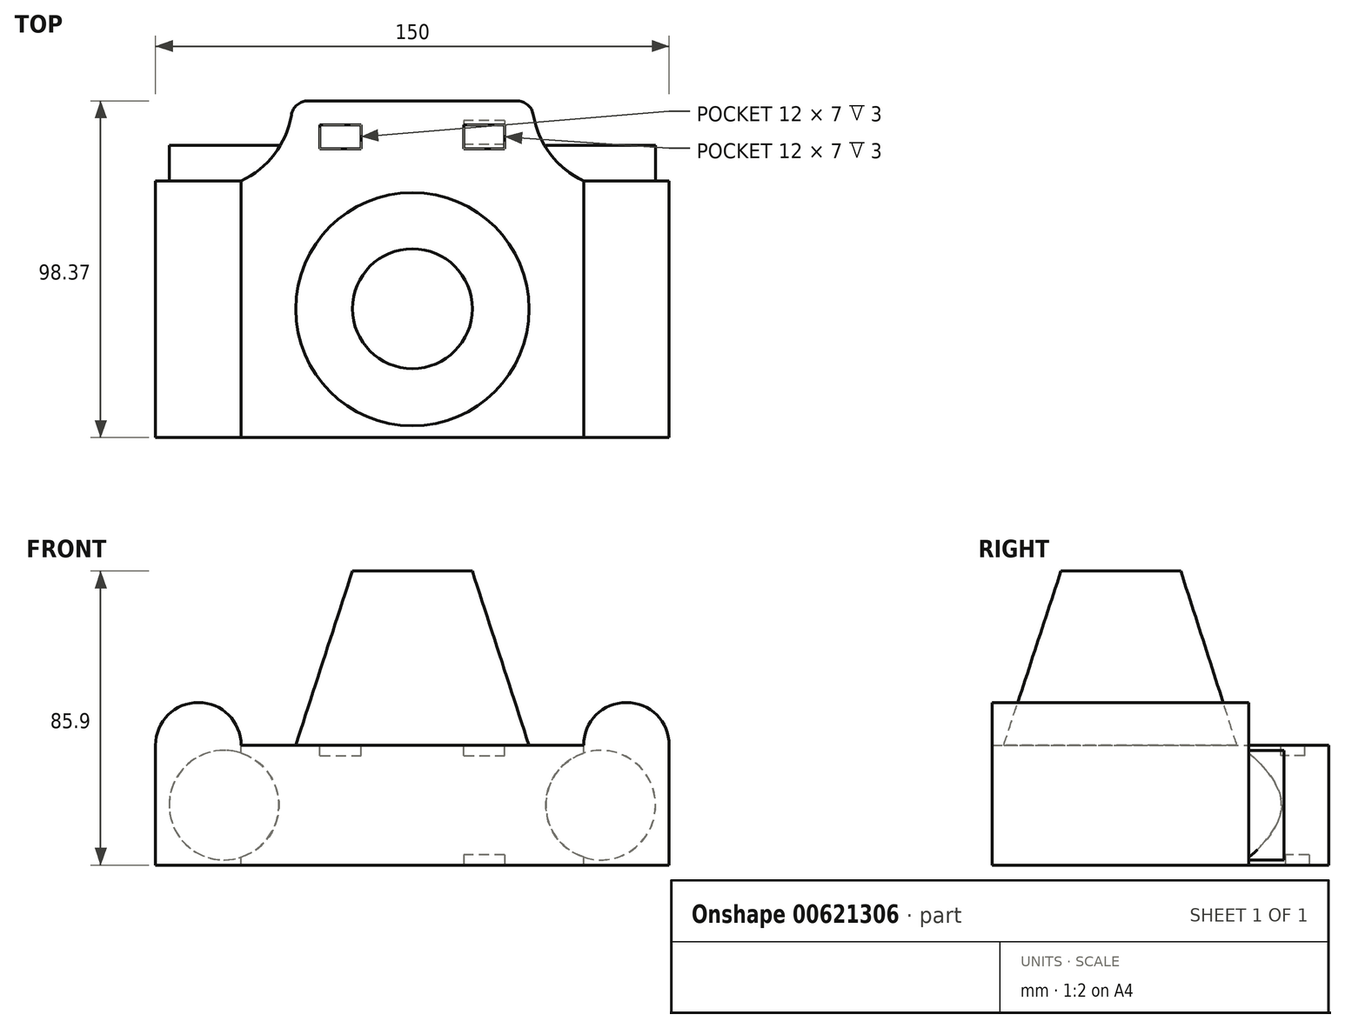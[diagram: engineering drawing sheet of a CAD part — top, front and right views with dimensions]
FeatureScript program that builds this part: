
annotation { "Feature Type Name" : "Feature", "Feature Type Description" : "" }
export const myFeature = defineFeature(function(context is Context, id is Id, definition is map)
    precondition{}
    {
        {
            var Q0;
            Q0=qCreatedBy(makeId("Front.planeOp"),FACE);
            var sketch = newSketch(context, id + "F0", { "sketchPlane" : qUnion([Q0])});
            skLineSegment(sketch, "E0.bottom", {"start": v(75, 17.5) * mm, "end": v(-75, 17.5) * mm});
            skLineSegment(sketch, "E0.top", {"start": v(75, -17.5) * mm, "end": v(-75, -17.5) * mm});
            skLineSegment(sketch, "E0.left", {"start": v(75, 17.5) * mm, "end": v(75, -17.5) * mm});
            skLineSegment(sketch, "E0.right", {"start": v(-75, 17.5) * mm, "end": v(-75, -17.5) * mm});
            skPoint(sketch, "E0.middle", {"position": v(0, 0) * mm});
            skArc(sketch, "E1", {"start": v(-50, 17.5) * mm, "mid": v(-62.5, 30) * mm, "end": v(-75, 17.5) * mm});
            skArc(sketch, "E2", {"start": v(75, 17.5) * mm, "mid": v(62.5, 30) * mm, "end": v(50, 17.5) * mm});
            skSolve(sketch);
        }
        {
            var Q0;
            Q0 = qSketchRegion(id + "F0", true);
            extrude(context, id + "F1", {"entities" : qUnion([Q0]), "depth" : 75 * mm, "offsetDistance" : 25 * mm});
        }
        {
            var Q0;
            Q0=makeQuery(id+"F1.opExtrude","SWEPT_FACE",FACE,{"disambiguationData":[OSD([sQuery(id+"F0.wireOp",EDGE,"E0.bottom")])]});
            var sketch = newSketch(context, id + "F2", { "sketchPlane" : qUnion([Q0])});
            skLineSegment(sketch, "E3", {"start": v(0, 0) * mm, "end": v(0, -75) * mm, "construction": true});
            skCircle(sketch, "E4", {"center": v(0, -37.5) * mm, "radius": 34.05 * mm});
            skSolve(sketch);
        }
        {
            var Q0;
            Q0=makeQuery(id+"F2.imprint","IMPRINT",FACE,{"disambiguationData":[TD([[makeQuery(id+"F2.imprint","IMPRINT",EDGE,{"derivedFrom":sQuery(id+"F2.wireOp",EDGE,"E4")}),1.0]])]});
            var sketch = newSketch(context, id + "F3", { "sketchPlane" : qUnion([Q0])});
            skLineSegment(sketch, "E5", {"start": v(0, 0) * mm, "end": v(0, -74.71) * mm, "construction": true});
            skCircle(sketch, "E6", {"center": v(0, -37.36) * mm, "radius": 3.44 * mm});
            skSolve(sketch);
        }
        {
            var Q0;
            Q0 = qSketchRegion(id + "F3", true);
            extrude(context, id + "F4", {"entities" : qUnion([Q0]), "operationType" : NewBodyOperationType.ADD, "depth" : 49.9 * mm, "offsetDistance" : 25 * mm});
        }
        {
            var Q0;
            Q0=makeQuery(id+"F4.opExtrude","CAP_FACE",FACE,{"disambiguationData":[OSD([sQuery(id+"F3.wireOp",EDGE,"E6")])],"isStart":false});
            var sketch = newSketch(context, id + "F5", { "sketchPlane" : qUnion([Q0])});
            skCircle(sketch, "E7", {"center": v(0, -37.36) * mm, "radius": 17.5 * mm});
            skSolve(sketch);
        }
        {
            var Q0;
            Q0 = qSketchRegion(id + "F5", true);
            extrude(context, id + "F6", {"entities" : qUnion([Q0]), "operationType" : NewBodyOperationType.ADD, "depth" : 1 * mm, "offsetDistance" : 25 * mm});
        }
        {
            var Q1;
            Q1=makeQuery(id+"F6.opExtrude","CAP_FACE",FACE,{"disambiguationData":[OSD([sQuery(id+"F5.wireOp",EDGE,"E7")])],"isStart":false});
            var Q2;
            Q2=makeQuery(id+"F2.imprint","IMPRINT",FACE,{"disambiguationData":[TD([[makeQuery(id+"F2.imprint","IMPRINT",EDGE,{"derivedFrom":sQuery(id+"F2.wireOp",EDGE,"E4")}),1.0]])]});
            loft(context, id + "F7", {"operationType" : NewBodyOperationType.ADD, "sheetProfilesArray" : [{ "sheetProfileEntities" : qUnion([Q1]) }, { "sheetProfileEntities" : qUnion([Q2]) }]});
        }
        {
            var Q0;
            Q0=makeQuery(id+"F1.opExtrude","SWEPT_FACE",FACE,{"disambiguationData":[OSD([sQuery(id+"F0.wireOp",EDGE,"E0.bottom")])]});
            var sketch = newSketch(context, id + "F8", { "sketchPlane" : qUnion([Q0])});
            skLineSegment(sketch, "E8.bottom", {"start": v(-35, -2.47) * mm, "end": v(35, -2.47) * mm});
            skLineSegment(sketch, "E8.top", {"start": v(-35, 23.37) * mm, "end": v(35, 23.37) * mm});
            skLineSegment(sketch, "E8.left", {"start": v(-35, -2.47) * mm, "end": v(-35, 23.37) * mm});
            skLineSegment(sketch, "E8.right", {"start": v(35, -2.47) * mm, "end": v(35, 23.37) * mm});
            skLineSegment(sketch, "E9", {"start": v(35, -2.47) * mm, "end": v(50, -2.47) * mm});
            skArc(sketch, "E10", {"start": v(-50, 0) * mm, "mid": v(-39.07, 9.49) * mm, "end": v(-35, 23.37) * mm});
            skArc(sketch, "E11", {"start": v(35, 23.37) * mm, "mid": v(39.07, 9.49) * mm, "end": v(50, 0) * mm});
            skLineSegment(sketch, "E12", {"start": v(-50, 0) * mm, "end": v(-35, 0) * mm});
            skLineSegment(sketch, "E13", {"start": v(-35, 0) * mm, "end": v(50, 0) * mm});
            skSolve(sketch);
        }
        {
            var Q0;
            Q0 = qSketchRegion(id + "F8", true);
            extrude(context, id + "F9", {"entities" : qUnion([Q0]), "operationType" : NewBodyOperationType.ADD, "oppositeDirection" : true, "depth" : 35 * mm, "offsetDistance" : 25 * mm});
        }
        {
            var Q0;
            Q0=makeQuery(id+"F9.opExtrude","SWEPT_EDGE",EDGE,{"disambiguationData":[OSD([sQuery(id+"F8.wireOp",EDGE,"E8.top"),sQuery(id+"F8.wireOp",EDGE,"E8.right"),sQuery(id+"F8.wireOp",EDGE,"E11")])]});
            var Q1;
            Q1=makeQuery(id+"F9.opExtrude","SWEPT_EDGE",EDGE,{"disambiguationData":[OSD([sQuery(id+"F8.wireOp",EDGE,"E8.top"),sQuery(id+"F8.wireOp",EDGE,"E8.left"),sQuery(id+"F8.wireOp",EDGE,"E10")])]});
            fillet(context, id + "F10", {"entities" : qUnion([Q0, Q1]), "radius" : 5 * mm, "tangentPropagation" : true, "allowEdgeOverflow" : false});
        }
        {
            var Q0;
            {var subQ0=sQuery(id+"F0.wireOp",EDGE,"E2");var subQ9=sQuery(id+"F0.wireOp",EDGE,"E0.left");var subQ10=sQuery(id+"F0.wireOp",EDGE,"E0.top");var subQ11=sQuery(id+"F0.wireOp",EDGE,"E0.bottom");Q0=makeQuery(id+"F9.boolean.opBoolean","SPLIT",FACE,{"disambiguationData":[TD([makeQuery(id+"F1.opExtrude","SWEPT_FACE",FACE,{"disambiguationData":[OSD([subQ9])]})])],"derivedFrom":makeQuery(id+"F1.opExtrude","CAP_FACE",FACE,{"disambiguationData":[OSD([subQ11,subQ10,subQ9,sQuery(id+"F0.wireOp",EDGE,"E0.right"),sQuery(id+"F0.wireOp",EDGE,"E1"),subQ0])],"isStart":true})});}
            var sketch = newSketch(context, id + "F11", { "sketchPlane" : qUnion([Q0])});
            skCircle(sketch, "E14", {"center": v(-55, 0) * mm, "radius": 16 * mm});
            skCircle(sketch, "E15", {"center": v(55, 0) * mm, "radius": 16 * mm});
            skSolve(sketch);
        }
        {
            var Q0;
            Q0 = qSketchRegion(id + "F11", true);
            extrude(context, id + "F12", {"entities" : qUnion([Q0]), "operationType" : NewBodyOperationType.ADD, "depth" : 10.3 * mm, "offsetDistance" : 25 * mm});
        }
        {
            var Q0;
            Q0=makeQuery(id+"F9.boolean.opBoolean","MERGE",FACE,{"derivedFrom":[makeQuery(id+"F1.opExtrude","SWEPT_FACE",FACE,{"disambiguationData":[OSD([sQuery(id+"F0.wireOp",EDGE,"E0.bottom")])]}),makeQuery(id+"F9.opExtrude","CAP_FACE",FACE,{"disambiguationData":[OSD([sQuery(id+"F8.wireOp",EDGE,"E8.bottom"),sQuery(id+"F8.wireOp",EDGE,"E8.top"),sQuery(id+"F8.wireOp",EDGE,"E8.left"),sQuery(id+"F8.wireOp",EDGE,"E8.right"),sQuery(id+"F8.wireOp",EDGE,"E10"),sQuery(id+"F8.wireOp",EDGE,"E11"),sQuery(id+"F8.wireOp",EDGE,"E12"),sQuery(id+"F8.wireOp",EDGE,"E13")])],"isStart":true})]});
            var sketch = newSketch(context, id + "F13", { "sketchPlane" : qUnion([Q0])});
            skLineSegment(sketch, "E16.bottom", {"start": v(15, 16.37) * mm, "end": v(27, 16.37) * mm});
            skLineSegment(sketch, "E16.top", {"start": v(15, 9.37) * mm, "end": v(27, 9.37) * mm});
            skLineSegment(sketch, "E16.left", {"start": v(15, 16.37) * mm, "end": v(15, 9.37) * mm});
            skLineSegment(sketch, "E16.right", {"start": v(27, 16.37) * mm, "end": v(27, 9.37) * mm});
            skLineSegment(sketch, "E17.bottom", {"start": v(-27, 16.37) * mm, "end": v(-15, 16.37) * mm});
            skLineSegment(sketch, "E17.top", {"start": v(-27, 9.37) * mm, "end": v(-15, 9.37) * mm});
            skLineSegment(sketch, "E17.left", {"start": v(-27, 16.37) * mm, "end": v(-27, 9.37) * mm});
            skLineSegment(sketch, "E17.right", {"start": v(-15, 16.37) * mm, "end": v(-15, 9.37) * mm});
            skSolve(sketch);
        }
        {
            var Q0;
            Q0 = qSketchRegion(id + "F13", true);
            extrude(context, id + "F14", {"entities" : qUnion([Q0]), "operationType" : NewBodyOperationType.REMOVE, "oppositeDirection" : true, "depth" : 3 * mm, "offsetDistance" : 25 * mm});
        }
        {
            var Q0;
            Q0=makeQuery(id+"F9.boolean.opBoolean","MERGE",FACE,{"derivedFrom":[makeQuery(id+"F1.opExtrude","SWEPT_FACE",FACE,{"disambiguationData":[OSD([sQuery(id+"F0.wireOp",EDGE,"E0.top")])]}),makeQuery(id+"F9.opExtrude","CAP_FACE",FACE,{"disambiguationData":[OSD([sQuery(id+"F8.wireOp",EDGE,"E8.bottom"),sQuery(id+"F8.wireOp",EDGE,"E8.top"),sQuery(id+"F8.wireOp",EDGE,"E8.left"),sQuery(id+"F8.wireOp",EDGE,"E8.right"),sQuery(id+"F8.wireOp",EDGE,"E10"),sQuery(id+"F8.wireOp",EDGE,"E11"),sQuery(id+"F8.wireOp",EDGE,"E12"),sQuery(id+"F8.wireOp",EDGE,"E13")])],"isStart":false})]});
            var sketch = newSketch(context, id + "F15", { "sketchPlane" : qUnion([Q0])});
            skLineSegment(sketch, "E18.bottom", {"start": v(27, -17.6) * mm, "end": v(15, -17.6) * mm});
            skLineSegment(sketch, "E18.top", {"start": v(27, -10.6) * mm, "end": v(15, -10.6) * mm});
            skLineSegment(sketch, "E18.left", {"start": v(27, -17.6) * mm, "end": v(27, -10.6) * mm});
            skLineSegment(sketch, "E18.right", {"start": v(15, -17.6) * mm, "end": v(15, -10.6) * mm});
            skSolve(sketch);
        }
        {
            var Q0;
            Q0 = qSketchRegion(id + "F15", true);
            extrude(context, id + "F16", {"entities" : qUnion([Q0]), "operationType" : NewBodyOperationType.REMOVE, "oppositeDirection" : true, "depth" : 3 * mm, "offsetDistance" : 25 * mm});
        }
    });
